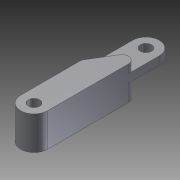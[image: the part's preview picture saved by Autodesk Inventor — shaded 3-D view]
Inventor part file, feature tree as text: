
AUTODESK INVENTOR PART (.ipt)
format: ipt  version: 2011 SP2 (Build 150309200, 309)  size: 125,440 bytes
history: native  units: mm
features: sketch x3, extrude x3, fillet x1, hole x1, projected_geometry x1
ambient origin geometry x8: Origin, YZ Plane, XZ Plane, XY Plane, X Axis, Y Axis, Z Axis, Center Point
feature tree (9):
  sketch  "Sketch1"  dims[d0=4.0mm d6=33.421041mm]
  extrude  "Extrusion2"  Depth=33.421041mm
  extrude  "Extrusion3"  Depth=10.0mm TaperAngle=0.0deg
  fillet  "Fillet1"  Radius=2.0mm
  hole  "Hole2"  [1 undecoded]
  extrude  "Extrusion4"  [1 undecoded]
  sketch  "Sketch3"  dims[d23=5.0mm d24=0.0mm d25=10.0mm d26=0.0mm d27=2.0mm]
  projected_geometry  "Projected Loop1"
  sketch  "Sketch4"  dims[d28=3.4mm d29=6.0mm d30=4.4mm d31=3.0mm d32=90.0deg d33=8.0mm d34=20.594885mm d35=10.0mm d36=0.0mm]
note: 2 required parameter values undecoded (feature->parameter linkage not recoverable at this tier; creation-order binding heuristic only, values carry confidence <= 0.55)
